# Revit family: Storage-Teknion-CW2BF_C+D_Two_Storage_Fridge_Credenza_29_Height_Low_Base-R2020
name_source: partatom
category: Furniture
units: mm (PartAtom-declared; Revit-internal decimal feet)

## family parameters
Always vertical = Yes
Cut with Voids When Loaded = No
OmniClass Number = 23.40.20.00
OmniClass Title = General Furniture and Specialties
Room Calculation Point = No
Shared = Yes
Work Plane-Based = No

## types (2) — shared parameters
Assembly Code = E2020200
Manufacturer = Teknion
Manufacturer Fax = 416.661.4586
Part Number = CW2BF
Product Documentation Link = https://www.teknion.com
Product Line = C+D Credenzas
Product Page URL = https://www.teknion.com
Series = C+D Conference Table
Sustainability Data = https://www.teknion.com
URL = www.teknion.com
Unit Weight URL = http://www.teknion.com
Warranty = http://www.teknion.com
zero-valued in all types: Default Elevation

## per-type parameters (varying)
| type | Description | Door Size | Gap A/V Cutout | Model | Width |
| Width 72" | C+D Two Storage Fridge Credenza, 29" Height, Low Base, 24" Depth, 72" Width | 17.642 " | 6.991 " | CW2B_2472 | 72 " |
| Width 60" | C+D Two Storage Fridge Credenza, 29" Height, Low Base, 24" Depth, 60" Width | 14.642 " | 3.991 " | CW2B_2460 | 60 " |

## geometry (parser evidence)
native form markers: Sweep x4
no freeform markers — native parametric forms only
